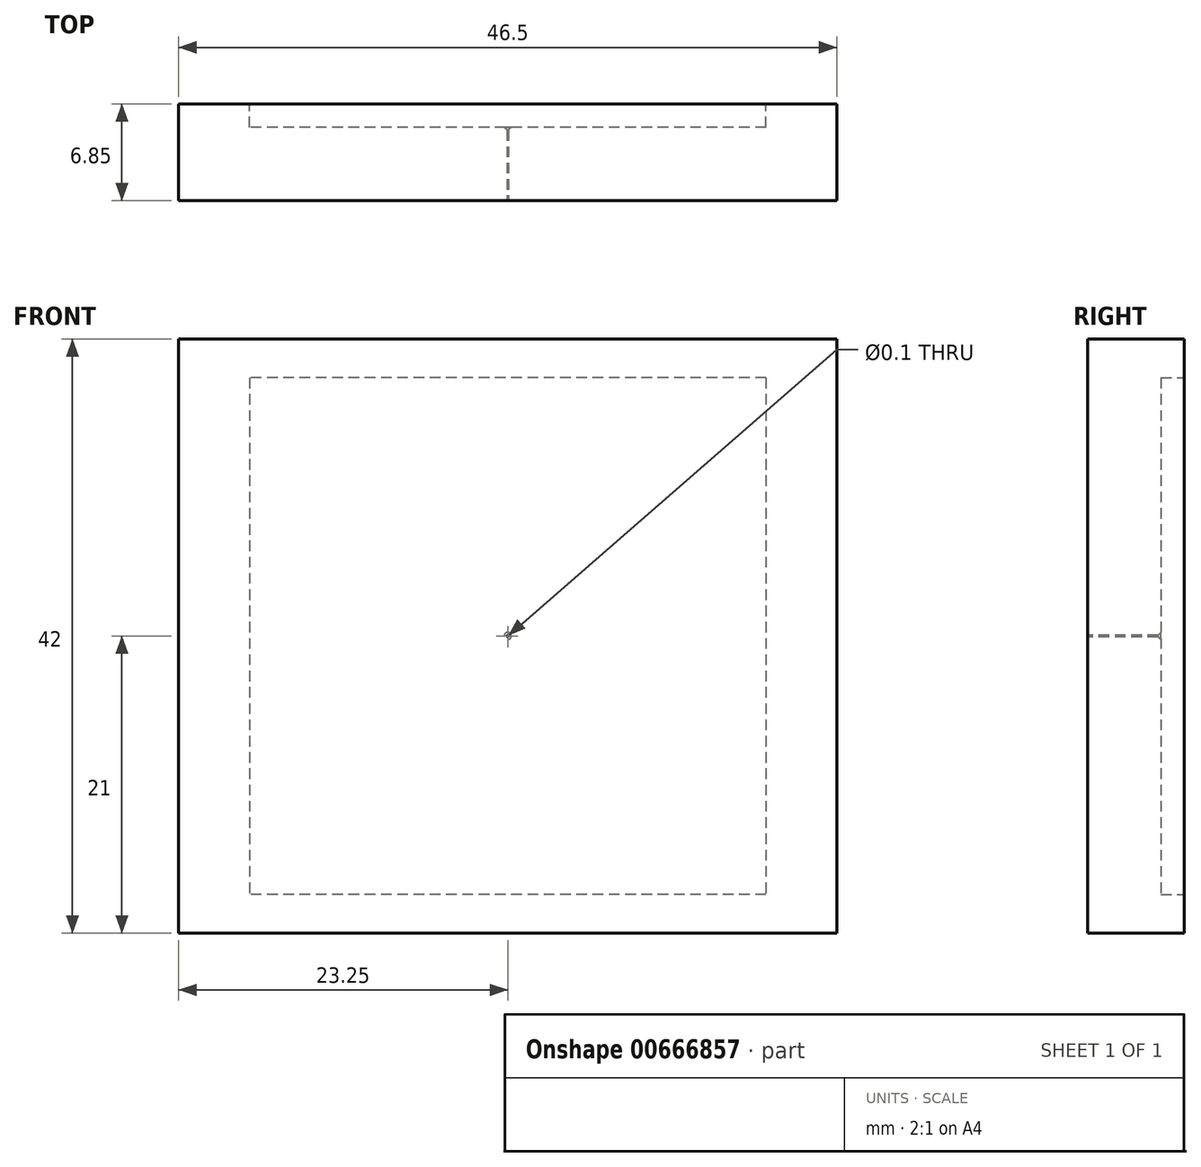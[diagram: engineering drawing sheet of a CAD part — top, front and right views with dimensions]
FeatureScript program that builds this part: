
annotation { "Feature Type Name" : "Feature", "Feature Type Description" : "" }
export const myFeature = defineFeature(function(context is Context, id is Id, definition is map)
    precondition{}
    {
        {
            var Q0;
            Q0=qCreatedBy(makeId("Front.planeOp"),FACE);
            var sketch = newSketch(context, id + "F0", { "sketchPlane" : qUnion([Q0])});
            skLineSegment(sketch, "E0.bottom", {"start": v(0, 0) * mm, "end": v(-46.5, 0) * mm});
            skLineSegment(sketch, "E0.top", {"start": v(0, 42) * mm, "end": v(-46.5, 42) * mm});
            skLineSegment(sketch, "E0.left", {"start": v(0, 0) * mm, "end": v(0, 42) * mm});
            skLineSegment(sketch, "E0.right", {"start": v(-46.5, 0) * mm, "end": v(-46.5, 42) * mm});
            skLineSegment(sketch, "E1", {"start": v(0, 42) * mm, "end": v(-5, 42) * mm, "construction": true});
            skLineSegment(sketch, "E2", {"start": v(-5, 42) * mm, "end": v(-5, 39.25) * mm, "construction": true});
            skLineSegment(sketch, "E3", {"start": v(-46.5, 0) * mm, "end": v(-41.5, 0) * mm, "construction": true});
            skLineSegment(sketch, "E4", {"start": v(-41.5, 0) * mm, "end": v(-41.5, 2.75) * mm, "construction": true});
            skLineSegment(sketch, "E5.bottom", {"start": v(-5, 39.25) * mm, "end": v(-41.5, 39.25) * mm});
            skLineSegment(sketch, "E5.top", {"start": v(-5, 2.75) * mm, "end": v(-41.5, 2.75) * mm});
            skLineSegment(sketch, "E5.left", {"start": v(-5, 39.25) * mm, "end": v(-5, 2.75) * mm});
            skLineSegment(sketch, "E5.right", {"start": v(-41.5, 39.25) * mm, "end": v(-41.5, 2.75) * mm});
            skSolve(sketch);
        }
        {
            var Q0;
            Q0 = qSketchRegion(id + "F0", true);
            var Q1;
            Q1=makeQuery(id+"F0.imprint","IMPRINT",FACE,{"disambiguationData":[TD([[makeQuery(id+"F0.imprint","IMPRINT",EDGE,{"derivedFrom":sQuery(id+"F0.wireOp",EDGE,"E5.bottom")}),1.0]])]});
            extrude(context, id + "F1", {"entities" : qUnion([Q0, Q1]), "depth" : 6.85 * mm, "offsetDistance" : 25 * mm});
        }
        {
            var Q0;
            Q0=makeQuery(id+"F0.imprint","IMPRINT",FACE,{"disambiguationData":[TD([[makeQuery(id+"F0.imprint","IMPRINT",EDGE,{"derivedFrom":sQuery(id+"F0.wireOp",EDGE,"E5.bottom")}),1.0]])]});
            extrude(context, id + "F2", {"entities" : qUnion([Q0]), "operationType" : NewBodyOperationType.REMOVE, "depth" : 1.66 * mm, "offsetDistance" : 25 * mm});
        }
        {
            var Q0;
            Q0=makeQuery(id+"F2.boolean.opBoolean","COPY",FACE,{"derivedFrom":makeQuery(id+"F2.opExtrude","CAP_FACE",FACE,{"disambiguationData":[OSD([sQuery(id+"F0.wireOp",EDGE,"E5.bottom"),sQuery(id+"F0.wireOp",EDGE,"E5.top"),sQuery(id+"F0.wireOp",EDGE,"E5.left"),sQuery(id+"F0.wireOp",EDGE,"E5.right")])],"isStart":false})});
            var sketch = newSketch(context, id + "F3", { "sketchPlane" : qUnion([Q0])});
            skLineSegment(sketch, "E6", {"start": v(23.25, 2.75) * mm, "end": v(23.25, 39.25) * mm, "construction": true});
            skPoint(sketch, "E7", {"position": v(23.25, 21) * mm});
            skSolve(sketch);
        }
        {
            var Q0;
            Q0=sQuery(id+"F3.wireOp",VERTEX,"E7");
            var Q1;
            Q1=makeQuery(id+"F1.opExtrude","SWEPT_BODY",BODY,{"disambiguationData":[OSD([sQuery(id+"F0.wireOp",EDGE,"E0.bottom"),sQuery(id+"F0.wireOp",EDGE,"E0.top"),sQuery(id+"F0.wireOp",EDGE,"E0.left"),sQuery(id+"F0.wireOp",EDGE,"E0.right")])]});
            hole(context, id + "F4", {"style" : HoleStyle.C_SINK, "endStyle" : HoleEndStyle.THROUGH, "holeDiameter" : 0.1 * mm, "cSinkDiameter" : 0.5 * mm, "cSinkAngle" : 90 * degree, "majorDiameter" : 5 * mm, "isTappedThrough" : true, "tappedDepth" : 12 * mm, "tapClearance" : 3, "locations" : qUnion([Q0]), "scope" : qUnion([Q1])});
        }
    });
